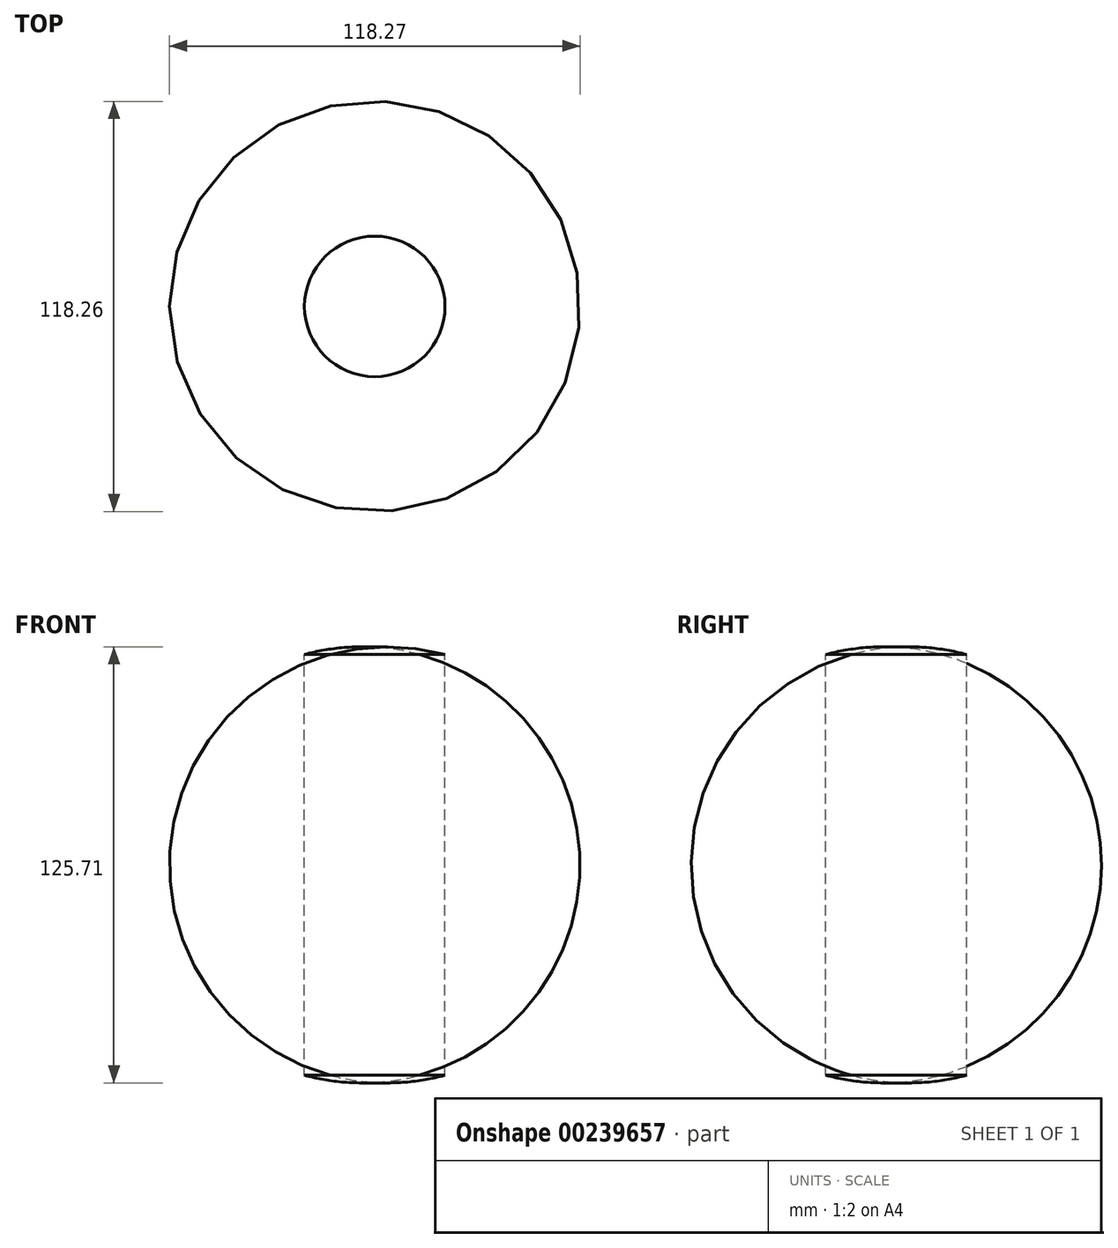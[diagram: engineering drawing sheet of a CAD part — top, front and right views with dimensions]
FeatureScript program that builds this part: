
annotation { "Feature Type Name" : "Feature", "Feature Type Description" : "" }
export const myFeature = defineFeature(function(context is Context, id is Id, definition is map)
    precondition{}
    {
        {
            var Q0;
            Q0=qCreatedBy(makeId("Front.planeOp"),FACE);
            var sketch = newSketch(context, id + "F0", { "sketchPlane" : qUnion([Q0])});
            skLineSegment(sketch, "E0", {"start": v(-40.68, 65.4) * mm, "end": v(-40.68, -54.08) * mm});
            skLineSegment(sketch, "E1", {"start": v(-20.41, 66) * mm, "end": v(-20.41, -55.28) * mm});
            skArc(sketch, "E2", {"start": v(-20.41, -55.28) * mm, "mid": v(25.9, 5.36) * mm, "end": v(-20.41, 66) * mm});
            skSolve(sketch);
        }
        {
            var Q0;
            Q0=makeQuery(id+"F0.imprint","IMPRINT",FACE,{"disambiguationData":[TD([[makeQuery(id+"F0.imprint","IMPRINT",EDGE,{"derivedFrom":sQuery(id+"F0.wireOp",EDGE,"E1")}),1.0]])]});
            var Q1;
            Q1=sQuery(id+"F0.wireOp",EDGE,"E0");
            revolve(context, id + "F1", {"entities" : qUnion([Q0]), "axis" : qUnion([Q1]), "revolveType" : RevolveType.FULL});
        }
    });
